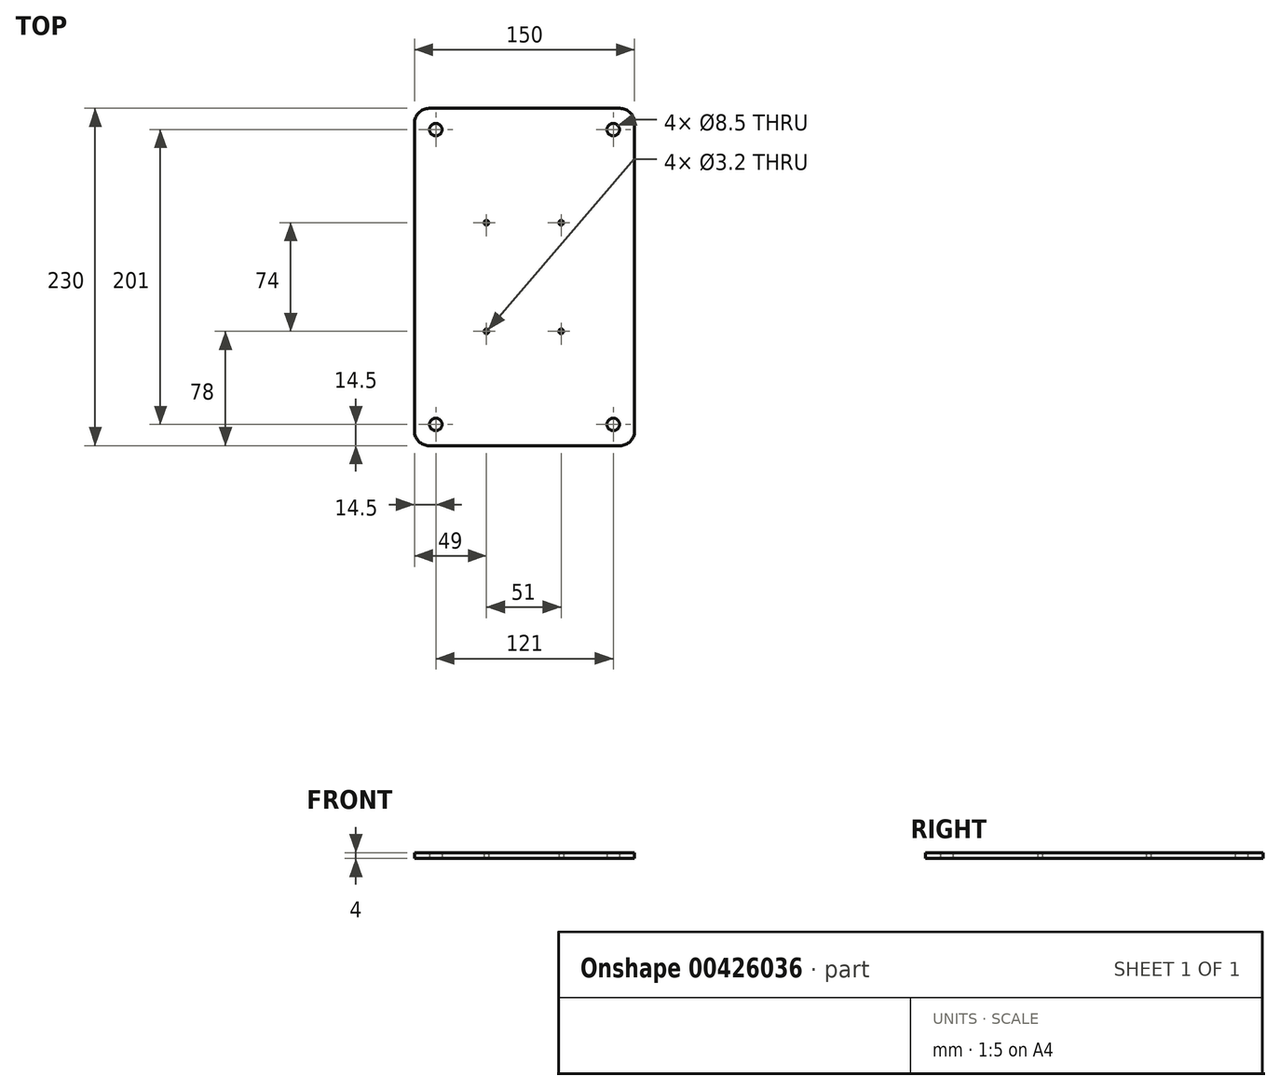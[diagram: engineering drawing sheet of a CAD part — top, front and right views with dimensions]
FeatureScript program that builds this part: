
annotation { "Feature Type Name" : "Feature", "Feature Type Description" : "" }
export const myFeature = defineFeature(function(context is Context, id is Id, definition is map)
    precondition{}
    {
        {
            var Q0;
            Q0=qCreatedBy(makeId("Top.planeOp"),FACE);
            var sketch = newSketch(context, id + "F0", { "sketchPlane" : qUnion([Q0])});
            skLineSegment(sketch, "E0.bottom", {"start": v(65, -115) * mm, "end": v(-65, -115) * mm});
            skLineSegment(sketch, "E0.top", {"start": v(65, 115) * mm, "end": v(-65, 115) * mm});
            skLineSegment(sketch, "E0.left", {"start": v(75, -105) * mm, "end": v(75, 105) * mm});
            skLineSegment(sketch, "E0.right", {"start": v(-75, -105) * mm, "end": v(-75, 105) * mm});
            skPoint(sketch, "E0.middle", {"position": v(0, 0) * mm});
            skPoint(sketch, "E1.visualSharp", {"position": v(-75, 115) * mm});
            skArc(sketch, "E1.filletArc", {"start": v(-65, 115) * mm, "mid": v(-72.07, 112.07) * mm, "end": v(-75, 105) * mm});
            skArc(sketch, "E2.MirrorCS", {"start": v(65, 115) * mm, "mid": v(72.07, 112.07) * mm, "end": v(75, 105) * mm});
            skPoint(sketch, "E3.MirrorP", {"position": v(75, 115) * mm});
            skArc(sketch, "E4.MirrorCS", {"start": v(-65, -115) * mm, "mid": v(-72.07, -112.07) * mm, "end": v(-75, -105) * mm});
            skArc(sketch, "E5.MirrorCS", {"start": v(65, -115) * mm, "mid": v(72.07, -112.07) * mm, "end": v(75, -105) * mm});
            skPoint(sketch, "E6.orphan", {"position": v(-75, -115) * mm});
            skPoint(sketch, "E7.orphan", {"position": v(75, -115) * mm});
            skCircle(sketch, "E8", {"center": v(-60.5, 100.5) * mm, "radius": 4.25 * mm});
            skCircle(sketch, "E9.MirrorC", {"center": v(60.5, 100.5) * mm, "radius": 4.25 * mm});
            skCircle(sketch, "E10.MirrorC", {"center": v(-60.5, -100.5) * mm, "radius": 4.25 * mm});
            skCircle(sketch, "E11.MirrorC", {"center": v(60.5, -100.5) * mm, "radius": 4.25 * mm});
            skCircle(sketch, "E12", {"center": v(25, 37) * mm, "radius": 1.6 * mm});
            skCircle(sketch, "E13.MirrorC", {"center": v(25, -37) * mm, "radius": 1.6 * mm});
            skCircle(sketch, "E14", {"center": v(-26, 37) * mm, "radius": 1.6 * mm});
            skCircle(sketch, "E15", {"center": v(-26, -37) * mm, "radius": 1.6 * mm});
            skSolve(sketch);
        }
        {
            var Q0;
            Q0=makeQuery(id+"F0.imprint","IMPRINT",FACE,{"disambiguationData":[TD([[makeQuery(id+"F0.imprint","IMPRINT",EDGE,{"derivedFrom":sQuery(id+"F0.wireOp",EDGE,"E0.bottom")}),-1.0]])]});
            extrude(context, id + "F1", {"entities" : qUnion([Q0]), "depth" : 4 * mm, "offsetDistance" : 25 * mm});
        }
    });
